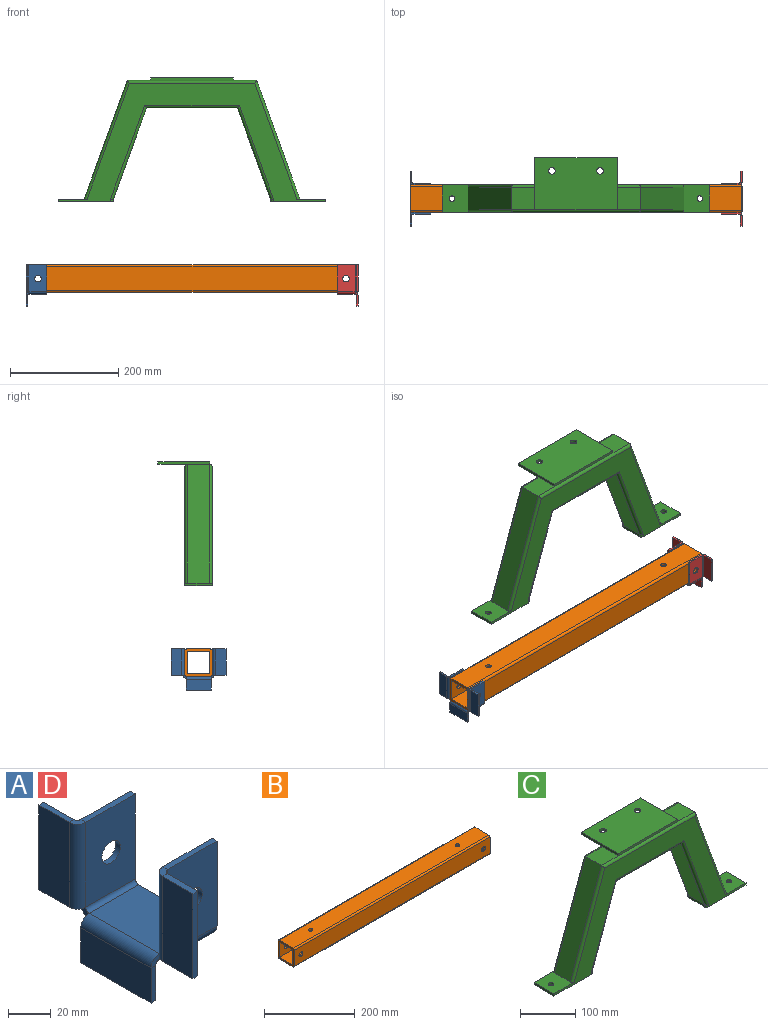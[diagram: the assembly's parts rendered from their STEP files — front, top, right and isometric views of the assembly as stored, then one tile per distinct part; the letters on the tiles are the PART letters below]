
ASSEMBLY  parts=4 mates=5
PART A: 48 faces, bbox 38.1x101.6x76.2 mm
  f0: plane 46.23x3.18mm, normal (1,0,0), area 146.8mm2, adj f1,f2,f18,f36
  f1: plane 46.23x32.64mm, normal (0,0,-1), area 1508.8mm2, adj f0,f19,f37,f47
  f2: plane 46.23x32.64mm, normal (0,0,1), area 1508.8mm2, adj f0,f20,f38,f46
  f3: plane 48.51x3.18mm, normal (1,0,0), area 154mm2, adj f5,f6,f7,f18
  f4: cylinder r=6.1mm len=12.19mm, axis (0,1,0), area 121.6mm2, adj f6,f7
  f5: plane 32.64x3.18mm, normal (0,0,1), area 103.6mm2, adj f3,f6,f7,f14
  f6: plane 48.51x32.64mm, normal (0,1,0), area 1466.7mm2, adj f3,f4,f5,f16,f19
  f7: plane 48.51x32.64mm, normal (0,-1,0), area 1466.7mm2, adj f3,f4,f5,f15,f20
  f8: plane 48.51x3.18mm, normal (0,1,0), area 154mm2, adj f9,f10,f11,f12
  f9: plane 19.94x3.18mm, normal (0,0,1), area 63.3mm2, adj f8,f11,f12,f14
  f10: plane 19.94x3.18mm, normal (0,0,-1), area 63.3mm2, adj f8,f11,f12,f13
  f11: plane 48.51x19.94mm, normal (1,0,0), area 967.3mm2, adj f8,f9,f10,f16
  f12: plane 48.51x19.94mm, normal (-1,0,0), area 967.3mm2, adj f8,f9,f10,f15
  f13: plane 5.46x5.46mm, normal (0,0,-1), area 19.3mm2, adj f10,f15,f16,f17
  f14: plane 5.46x5.46mm, normal (0,0,1), area 19.3mm2, adj f5,f9,f15,f16
  f15: cylinder r=5.46mm len=48.51mm, axis (0,0,-1), area 416.2mm2, adj f7,f12,f13,f14
  f16: cylinder r=2.29mm len=48.51mm, axis (0,0,-1), area 174.2mm2, adj f6,f11,f13,f14
  f17: plane 5.46x5.46mm, normal (-1,0,0), area 19.3mm2, adj f13,f19,f20,f44
  f18: plane 5.46x5.46mm, normal (1,0,0), area 19.3mm2, adj f0,f3,f19,f20
  f19: cylinder r=5.46mm len=32.64mm, axis (-1,0,0), area 280mm2, adj f1,f6,f17,f18
  f20: cylinder r=2.29mm len=32.64mm, axis (-1,0,0), area 117.2mm2, adj f2,f7,f17,f18
  f21: plane 48.51x3.18mm, normal (1,0,0), area 154mm2, adj f22,f24,f25,f36
  f22: plane 32.64x3.18mm, normal (0,0,1), area 103.6mm2, adj f21,f24,f25,f32
  f23: cylinder r=6.1mm len=12.19mm, axis (0,1,0), area 121.6mm2, adj f24,f25
  f24: plane 48.51x32.64mm, normal (0,-1,0), area 1466.7mm2, adj f21,f22,f23,f34,f37
  f25: plane 48.51x32.64mm, normal (0,1,0), area 1466.7mm2, adj f21,f22,f23,f33,f38
  f26: plane 48.51x3.18mm, normal (0,-1,0), area 154mm2, adj f27,f28,f29,f30
  f27: plane 19.94x3.18mm, normal (0,0,-1), area 63.3mm2, adj f26,f29,f30,f31
  f28: plane 19.94x3.18mm, normal (0,0,1), area 63.3mm2, adj f26,f29,f30,f32
  f29: plane 48.51x19.94mm, normal (1,0,0), area 967.3mm2, adj f26,f27,f28,f34
  f30: plane 48.51x19.94mm, normal (-1,0,0), area 967.3mm2, adj f26,f27,f28,f33
  f31: plane 5.46x5.46mm, normal (0,0,-1), area 19.3mm2, adj f27,f33,f34,f35
  f32: plane 5.46x5.46mm, normal (0,0,1), area 19.3mm2, adj f22,f28,f33,f34
  f33: cylinder r=5.46mm len=48.51mm, axis (0,0,-1), area 416.2mm2, adj f25,f30,f31,f32
  f34: cylinder r=2.29mm len=48.51mm, axis (0,0,-1), area 174.2mm2, adj f24,f29,f31,f32
  f35: plane 5.46x5.46mm, normal (-1,0,0), area 19.3mm2, adj f31,f37,f38,f45
  f36: plane 5.46x5.46mm, normal (1,0,0), area 19.3mm2, adj f0,f21,f37,f38
  f37: cylinder r=5.46mm len=32.64mm, axis (-1,0,0), area 280mm2, adj f1,f24,f35,f36
  f38: cylinder r=2.29mm len=32.64mm, axis (-1,0,0), area 117.2mm2, adj f2,f25,f35,f36
  f39: plane 46.23x3.18mm, normal (0,0,-1), area 146.8mm2, adj f40,f41,f42,f43
  f40: plane 19.94x3.18mm, normal (0,1,0), area 63.3mm2, adj f39,f42,f43,f44
  f41: plane 19.94x3.18mm, normal (0,-1,0), area 63.3mm2, adj f39,f42,f43,f45
  f42: plane 46.23x19.94mm, normal (1,0,0), area 921.7mm2, adj f39,f40,f41,f47
  f43: plane 46.23x19.94mm, normal (-1,0,0), area 921.7mm2, adj f39,f40,f41,f46
  f44: plane 5.46x5.46mm, normal (0,1,0), area 19.3mm2, adj f17,f40,f46,f47
  f45: plane 5.46x5.46mm, normal (0,-1,0), area 19.3mm2, adj f35,f41,f46,f47
  f46: cylinder r=5.46mm len=46.23mm, axis (0,1,0), area 396.5mm2, adj f2,f43,f44,f45
  f47: cylinder r=2.29mm len=46.23mm, axis (0,1,0), area 166mm2, adj f1,f42,f44,f45
PART B: 22 faces, bbox 609.6x50.8x50.8 mm
  f0: plane 609.6x43.18mm, normal (0,0,-1), area 24739.1mm2, adj f9,f11,f12,f13,f18,f19
  f1: plane 609.6x41.28mm, normal (0,0,1), area 23577.8mm2, adj f4,f5,f12,f13,f18,f19
  f2: plane 609.6x43.18mm, normal (0,1,0), area 26089mm2, adj f6,f11,f12,f13,f14,f15
  f3: plane 609.6x43.18mm, normal (0,-1,0), area 26089mm2, adj f8,f9,f12,f13,f16,f17
  f4: plane 609.6x41.28mm, normal (0,1,0), area 24927.7mm2, adj f1,f10,f12,f13,f16,f17
  f5: plane 609.6x41.28mm, normal (0,-1,0), area 24927.7mm2, adj f1,f10,f12,f13,f14,f15
  f6: cylinder r=3.81mm len=609.6mm, axis (-1,0,0), area 3648.3mm2, adj f2,f7,f12,f13
  f7: plane 609.6x43.18mm, normal (0,0,1), area 26160.4mm2, adj f6,f8,f12,f13,f20,f21
  f8: cylinder r=3.81mm len=609.6mm, axis (-1,0,0), area 3648.3mm2, adj f3,f7,f12,f13
  f9: cylinder r=3.81mm len=609.6mm, axis (-1,0,0), area 3648.3mm2, adj f0,f3,f12,f13
  f10: plane 609.6x41.28mm, normal (0,0,-1), area 24999.1mm2, adj f4,f5,f12,f13,f20,f21
  f11: cylinder r=3.81mm len=609.6mm, axis (-1,0,0), area 3648.3mm2, adj f0,f2,f12,f13
  f12: plane 50.8x50.8mm, normal (1,0,0), area 864.6mm2, adj f0,f1,f2,f3,f4,f5,f6,f7
  f13: plane 50.8x50.8mm, normal (-1,0,0), area 864.6mm2, adj f0,f1,f2,f3,f4,f5,f6,f7
  f14: cylinder r=6.1mm len=12.19mm, axis (0,-1,0), area 182.4mm2, adj f2,f5
  f15: cylinder r=6.1mm len=12.19mm, axis (0,-1,0), area 182.4mm2, adj f2,f5
  f16: cylinder r=6.1mm len=12.19mm, axis (0,-1,0), area 182.4mm2, adj f3,f4
  f17: cylinder r=6.1mm len=12.19mm, axis (0,-1,0), area 182.4mm2, adj f3,f4
  f18: cylinder r=15.88mm len=31.75mm, axis (0,0,-1), area 475mm2, adj f0,f1
  f19: cylinder r=15.88mm len=31.75mm, axis (0,0,-1), area 475mm2, adj f0,f1
  f20: cylinder r=5.08mm len=10.16mm, axis (0,0,-1), area 152mm2, adj f7,f10
  f21: cylinder r=5.08mm len=10.16mm, axis (0,0,-1), area 152mm2, adj f7,f10
PART C: 57 faces, bbox 493.3x100.3x228.6 mm
  f0: plane 43.19x40.64mm, normal (0,0,1), area 1755mm2, adj f4,f6,f19,f42
  f1: cylinder r=5.08mm len=174.74mm, axis (1,0,0), area 1358.3mm2, adj f2,f13,f14,f15
  f2: plane 167.63x40.64mm, normal (0,0,-1), area 6812.5mm2, adj f1,f3,f12,f16
  f3: cylinder r=5.08mm len=174.74mm, axis (1,0,0), area 1358.3mm2, adj f2,f10,f11,f17
  f4: cylinder r=5.08mm len=238.77mm, axis (1,0,0), area 1884.7mm2, adj f0,f5,f9,f10,f18,f41
  f5: plane 43.19x40.64mm, normal (0,0,1), area 1755mm2, adj f4,f6,f8,f40
  f6: cylinder r=5.08mm len=238.77mm, axis (1,0,0), area 1884.7mm2, adj f0,f5,f7,f14,f20,f39
  f7: cylinder r=5.08mm len=220.81mm, axis (0.34,0,0.94), area 1844.7mm2, adj f6,f8,f14,f30
  f8: plane 219.08x79.74mm, normal (-0.94,0,0.34), area 9474.6mm2, adj f5,f7,f9,f30
  f9: cylinder r=5.08mm len=220.81mm, axis (0.34,0,0.94), area 1844.7mm2, adj f4,f8,f10,f30
  f10: plane 493.32x218.76mm, normal (0,-1,0), area 25929.6mm2, adj f3,f4,f9,f11,f17,f18,f21,f23
  f11: cylinder r=5.08mm len=175.09mm, axis (0.34,0,0.94), area 1444.6mm2, adj f3,f10,f12,f31
  f12: plane 168.28x61.25mm, normal (0.94,0,-0.34), area 7277.6mm2, adj f2,f11,f13,f28
  f13: cylinder r=5.08mm len=175.09mm, axis (0.34,0,0.94), area 1444.6mm2, adj f1,f12,f14,f32
  f14: plane 493.32x218.76mm, normal (0,1,0), area 25929.6mm2, adj f1,f6,f7,f13,f15,f20,f21,f23
  f15: cylinder r=5.08mm len=175.09mm, axis (0.34,0,-0.94), area 1444.6mm2, adj f1,f14,f16,f26
  f16: plane 168.28x61.25mm, normal (-0.94,0,-0.34), area 7277.6mm2, adj f2,f15,f17,f22
  f17: cylinder r=5.08mm len=175.09mm, axis (0.34,0,-0.94), area 1444.6mm2, adj f3,f10,f16,f24
  f18: cylinder r=5.08mm len=220.81mm, axis (0.34,0,-0.94), area 1844.7mm2, adj f4,f10,f19,f25
  f19: plane 219.08x79.74mm, normal (0.94,0,0.34), area 9474.6mm2, adj f0,f18,f20,f25
  f20: cylinder r=5.08mm len=220.81mm, axis (0.34,0,-0.94), area 1844.7mm2, adj f6,f14,f19,f25
  f21: plane 101.6x50.8mm, normal (0,0,-1), area 5069.1mm2, adj f10,f14,f22,f23,f35,f36,f38
  f22: plane 40.64x4.76mm, normal (-1,0,0), area 193.5mm2, adj f16,f21,f35,f36
  f23: plane 50.8x4.76mm, normal (1,0,0), area 241.9mm2, adj f10,f14,f21,f25
  f24: plane 5.41x5.08mm, normal (0,0,1), area 0.4mm2, adj f10,f17,f35
  f25: plane 52.95x50.8mm, normal (0,0,1), area 2345.7mm2, adj f10,f14,f18,f19,f20,f23,f38
  f26: plane 5.41x5.08mm, normal (0,0,1), area 0.4mm2, adj f14,f15,f36
  f27: plane 101.6x50.8mm, normal (0,0,-1), area 5069.1mm2, adj f10,f14,f28,f29,f33,f34,f37
  f28: plane 40.64x4.76mm, normal (1,0,0), area 193.5mm2, adj f12,f27,f33,f34
  f29: plane 50.8x4.76mm, normal (-1,0,0), area 241.9mm2, adj f10,f14,f27,f30
  f30: plane 52.95x50.8mm, normal (0,0,1), area 2345.7mm2, adj f7,f8,f9,f10,f14,f29,f37
  f31: plane 5.41x5.08mm, normal (0,0,1), area 0.4mm2, adj f10,f11,f34
  f32: plane 5.41x5.08mm, normal (0,0,1), area 0.4mm2, adj f13,f14,f33
  f33: cylinder r=5.08mm len=5.08mm, axis (0,0,1), area 38mm2, adj f14,f27,f28,f32
  f34: cylinder r=5.08mm len=5.08mm, axis (0,0,1), area 38mm2, adj f10,f27,f28,f31
  f35: cylinder r=5.08mm len=5.08mm, axis (0,0,-1), area 38mm2, adj f10,f21,f22,f24
  f36: cylinder r=5.08mm len=5.08mm, axis (0,0,-1), area 38mm2, adj f14,f21,f22,f26
  f37: cylinder r=5.08mm len=10.16mm, axis (0,0,-1), area 152mm2, adj f27,f30
  f38: cylinder r=5.08mm len=10.16mm, axis (0,0,-1), area 152mm2, adj f21,f25
  f39: plane 152.4x54.61mm, normal (0,0,-1), area 8089.1mm2, adj f6,f40,f42,f43,f45,f46
  f40: plane 95.25x4.76mm, normal (-1,0,0), area 453.6mm2, adj f5,f39,f41,f43,f44
  f41: plane 152.4x4.76mm, normal (0,-1,0), area 725.8mm2, adj f4,f40,f42,f44
  f42: plane 95.25x4.76mm, normal (1,0,0), area 453.6mm2, adj f0,f39,f41,f43,f44
  f43: plane 152.4x4.76mm, normal (0,1,0), area 725.8mm2, adj f39,f40,f42,f44
  f44: plane 152.4x95.25mm, normal (0,0,1), area 14282.6mm2, adj f40,f41,f42,f43,f45,f46
  f45: cylinder r=6.1mm len=12.19mm, axis (0,0,1), area 182.4mm2, adj f39,f44
  f46: cylinder r=6.1mm len=12.19mm, axis (0,0,1), area 182.4mm2, adj f39,f44
  f47: plane 214.31x78mm, normal (-0.94,0,-0.34), area 9413.4mm2, adj f48,f51,f53,f55
  f48: plane 43.92x41.28mm, normal (0,0,1), area 1813mm2, adj f47,f49,f53,f55
  f49: plane 173.04x62.98mm, normal (0.94,0,0.34), area 7600.5mm2, adj f48,f50,f53,f55
  f50: plane 174.3x41.28mm, normal (0,0,1), area 7194.2mm2, adj f49,f53,f54,f55
  f51: plane 232.1x41.28mm, normal (0,0,-1), area 9580mm2, adj f47,f52,f53,f55
  f52: plane 214.31x78mm, normal (0.94,0,-0.34), area 9413.4mm2, adj f51,f53,f55,f56
  f53: plane 388.11x214.31mm, normal (0,-1,0), area 25401mm2, adj f47,f48,f49,f50,f51,f52,f54,f56
  f54: plane 173.04x62.98mm, normal (-0.94,0,0.34), area 7600.5mm2, adj f50,f53,f55,f56
  f55: plane 388.11x214.31mm, normal (0,1,0), area 25401mm2, adj f47,f48,f49,f50,f51,f52,f54,f56
  f56: plane 43.92x41.28mm, normal (0,0,1), area 1813mm2, adj f52,f53,f54,f55
PART D: same geometry as A
PLACE A t=(-384.13,49.85,45.32)mm
PLACE B t=(-382.54,49.85,45.32)mm
PLACE C t=(-77.74,49.85,182.54)mm
PLACE D rot(axis=(0,0,-1),180deg) t=(228.65,49.85,45.32)mm
MATE planar A.f7 <-> B.f2  axis (0,-1,0) through (-362.38,75.25,46.55)mm
MATE planar A.f2 <-> B.f0  axis (0,0,1) through (-346.03,49.85,19.92)mm
MATE planar B.f0 <-> D.f2  axis (0,0,-1) through (-77.74,49.85,19.92)mm
MATE cylindrical C.f38 <-> B.f20  axis (0,0,-1) through (150.86,49.85,187.3)mm
MATE planar D.f25 <-> B.f15  axis (0,-1,0) through (223.19,75.25,70.72)mm
